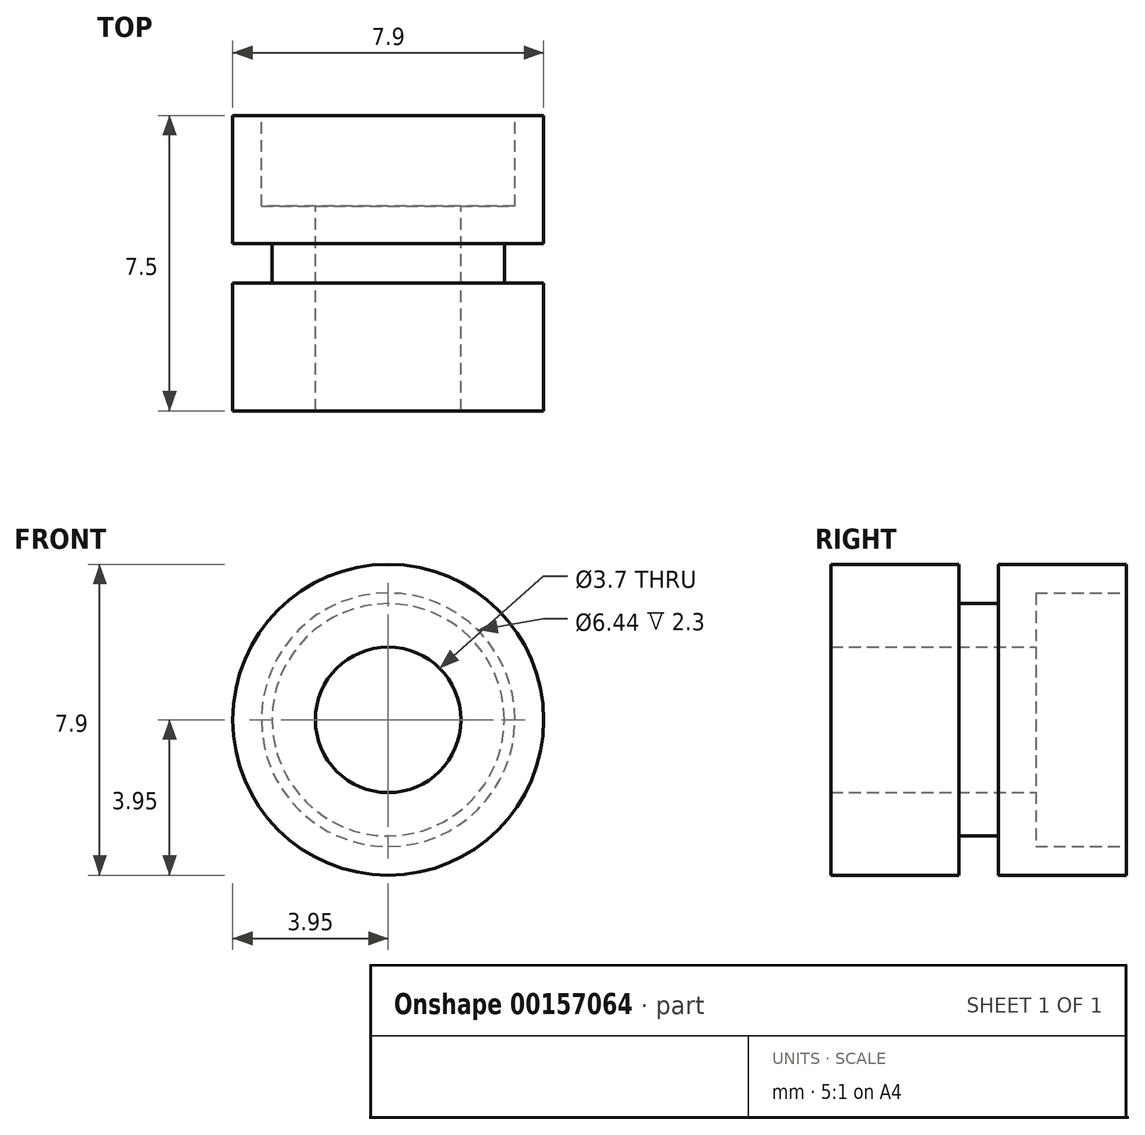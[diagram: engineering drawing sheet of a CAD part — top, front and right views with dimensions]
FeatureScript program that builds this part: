
annotation { "Feature Type Name" : "Feature", "Feature Type Description" : "" }
export const myFeature = defineFeature(function(context is Context, id is Id, definition is map)
    precondition{}
    {
        {
            var Q0;
            Q0=qCreatedBy(makeId("Right.planeOp"),FACE);
            var sketch = newSketch(context, id + "F0", { "sketchPlane" : qUnion([Q0])});
            skLineSegment(sketch, "E0", {"start": v(11.47, 0) * mm, "end": v(0, 0) * mm, "construction": true});
            skLineSegment(sketch, "E1", {"start": v(5.2, 1.85) * mm, "end": v(0, 1.85) * mm});
            skLineSegment(sketch, "E2", {"start": v(5.2, 1.85) * mm, "end": v(5.2, 3.22) * mm});
            skLineSegment(sketch, "E3", {"start": v(7.5, 3.22) * mm, "end": v(5.2, 3.22) * mm});
            skLineSegment(sketch, "E4", {"start": v(7.5, 3.22) * mm, "end": v(7.5, 3.95) * mm});
            skLineSegment(sketch, "E5", {"start": v(4.25, 3.95) * mm, "end": v(7.5, 3.95) * mm});
            skLineSegment(sketch, "E6", {"start": v(4.25, 3.95) * mm, "end": v(4.25, 2.95) * mm});
            skLineSegment(sketch, "E7", {"start": v(3.25, 2.95) * mm, "end": v(4.25, 2.95) * mm});
            skLineSegment(sketch, "E8", {"start": v(3.25, 2.95) * mm, "end": v(3.25, 3.95) * mm});
            skLineSegment(sketch, "E9", {"start": v(0, 3.95) * mm, "end": v(3.25, 3.95) * mm});
            skLineSegment(sketch, "E10", {"start": v(0, 3.95) * mm, "end": v(0, 1.85) * mm});
            skSolve(sketch);
        }
        {
            var Q0;
            Q0=makeQuery(id+"F0.imprint","IMPRINT",FACE,{"disambiguationData":[TD([[makeQuery(id+"F0.imprint","IMPRINT",EDGE,{"derivedFrom":sQuery(id+"F0.wireOp",EDGE,"E1")}),-1.0]])]});
            var Q1;
            Q1=sQuery(id+"F0.wireOp",EDGE,"E0");
            revolve(context, id + "F1", {"entities" : qUnion([Q0]), "axis" : qUnion([Q1]), "revolveType" : RevolveType.FULL});
        }
    });
